# Revit family: Faucet-Handle-KOHLER-COMPONENTS-K-77981T
name_source: partatom
category: Plumbing Fixtures
revit_build: Autodesk Revit 2017 (Build: 20160225_1515(x64)
units: mm (PartAtom-declared; Revit-internal decimal feet)

## family parameters
Cut with Voids When Loaded = No
Host = Face
OmniClass Number = 23.31.11.00
OmniClass Title = Faucets
Part Type = Normal
Room Calculation Point = No
Round Connector Dimension = Use Diameter
Shared = No

## types (21) — shared parameters
ADA Compliant = No
Assembly Code = D2010
CW Connection = Yes
Cold Water Inlet = Cold Water Inlet
Date Modified = 09/08/2020
Default Elevation = 36"
Drain Included = No
Flow Rate = 0 GPM
HW Connection = Yes
Hot Water Inlet = Hot Water Inlet
Manufacturer = KOHLER Co.
Master Format 2014 = 22.41.39
Master Format 2014 Name = Residential Faucets, Supplies, and Trim
Material = Premium Metal Construction
Pressure = 0.00 psi
Product Documentation Link = https://files.kohler.com.cn
Product Name = COMPONENTS
Product Page URL = https://www.kohler.com.cn
URL = http://www.kohler.com.cn
Vent Connection = No
Waste Connection = No
Waste Water Outlet = Waste Water Outlet
WaterSense Certified = No

## per-type parameters (varying)
| type | Description | Dist | Dist_1 | Finish | Handle Clearance | Height | Ind Handle | Length | Lever Handle | Model | Oyl Handle | Type |
| Lever Handle, CP-Polished Chrome | Double-handle wall outlet basin faucet handle lever type | 0" | 2 3/8" | Kohler-Metal-CP-Polished_Chrome | 2 5/16" | 2 3/8" | No | 1 9/16" | Yes | K-77981T-4-CP | No | 1 |
| Lever Handle, BN-Roman Silver | Double-handle wall outlet basin faucet handle lever type | 0" | 2 3/8" | Kohler-Metal-BN-Roman_Silver | 2 5/16" | 2 3/8" | No | 1 9/16" | Yes | K-77981T-4-BN | No | 3 |
| Lever Handle, 2BL-Original Black | Double-handle wall outlet basin faucet handle lever type | 0" | 2 3/8" | Kohler-Metal-2BL-Original_Black | 2 5/16" | 2 3/8" | No | 1 9/16" | Yes | K-77981T-4-2BL | No | 5 |
| Oyl Handle, CP-Polished Chrome | Double-handle wall outlet basin faucet handle post type | 1 3/16" | 0" | Kohler-Metal-CP-Polished_Chrome | 2 3/8" | 2 3/8" | No | 1 1/2" | No | K-77981T-8-CP | Yes | 8 |
| Oyl Handle, BN-Roman Silver | Double-handle wall outlet basin faucet handle post type | 1 3/16" | 0" | Kohler-Metal-BN-Roman_Silver | 2 3/8" | 2 3/8" | No | 1 1/2" | No | K-77981T-8-BN | Yes | 10 |
| Oyl Handle, 2BL-Original_Black | Double-handle wall outlet basin faucet handle post type | 1 3/16" | 0" | Kohler-Metal-2BL-Original_Black | 2 3/8" | 2 3/8" | No | 1 1/2" | No | K-77981T-8-2BL | Yes | 12 |
| Industrial Handle, CP-Polished Chrome | Double Handle Wall Outlet Basin Faucet Handle-Wheel Type | 1 3/8" | 2 3/8" | Kohler-Metal-CP-Polished_Chrome | 2 3/4" | 2 3/4" | Yes | 1 3/4" | No | K-77981T-9-CP | No | 15 |
| Industrial Handle, BN-Roman Silver | Double Handle Wall Outlet Basin Faucet Handle-Wheel Type | 1 3/8" | 2 3/8" | Kohler-Metal-BN-Roman_Silver | 2 3/4" | 2 3/4" | Yes | 1 3/4" | No | K-77981T-9-BN | No | 17 |
| Industrial Handle,2MB-Vibrant Brushed Moderne Brass | Double Handle Wall Outlet Basin Faucet Handle-Wheel Type | 1 3/8" | 2 3/8" | Kohler-Metal-2MB-Vibrant_Brushed_Moderne_Brass | 2 3/4" | 2 3/4" | Yes | 1 3/4" | No | K-77981T-9-2MB | No | 21 |
| Lever Handle, AF-Flange Gold | Double-handle wall outlet basin faucet handle lever type | 0" | 2 3/8" | Kohler-Metal-AF-Flange_Gold | 2 5/16" | 2 3/8" | No | 1 9/16" | Yes | K-77981T-4-AF | No | 2 |
| Lever Handle, RGD-Rose Gold | Double-handle wall outlet basin faucet handle lever type | 0" | 2 3/8" | Kohler-Metal-RGD-Rose_Gold | 2 5/16" | 2 3/8" | No | 1 9/16" | Yes | K-77981T-4-RGD | No | 4 |
| Lever Handle, TT-Titanium Silver | Double-handle wall outlet basin faucet handle lever type | 0" | 2 3/8" | Kohler-Metal-TT-Titanium_Silver | 2 5/16" | 2 3/8" | No | 1 9/16" | Yes | K-77981T-4-TT | No | 6 |
| Oyl Handle, AF-Flange Gold | Double-handle wall outlet basin faucet handle post type | 1 3/16" | 0" | Kohler-Metal-AF-Flange_Gold | 2 3/8" | 2 3/8" | No | 1 1/2" | No | K-77981T-8-AF | Yes | 9 |
| Oyl Handle, RGD-Rose Gold | Double-handle wall outlet basin faucet handle post type | 1 3/16" | 0" | Kohler-Metal-RGD-Rose_Gold | 2 3/8" | 2 3/8" | No | 1 1/2" | No | K-77981T-8-RGD | Yes | 11 |
| Oyl Handle, TT-Titanium Silver | Double-handle wall outlet basin faucet handle post type | 1 3/16" | 0" | Kohler-Metal-TT-Titanium_Silver | 2 3/8" | 2 3/8" | No | 1 1/2" | No | K-77981T-8-TT | Yes | 13 |
| Industrial Handle, AF-Flange Gold | Double Handle Wall Outlet Basin Faucet Handle-Wheel Type | 1 3/8" | 2 3/8" | Kohler-Metal-AF-Flange_Gold | 2 3/4" | 2 3/4" | Yes | 1 3/4" | No | K-77981T-9-AF | No | 16 |
| Industrial Handle, RGD-Rose Gold | Double Handle Wall Outlet Basin Faucet Handle-Wheel Type | 1 3/8" | 2 3/8" | Kohler-Metal-RGD-Rose_Gold | 2 3/4" | 2 3/4" | Yes | 1 3/4" | No | K-77981T-9-RGD | No | 18 |
| Industrial Handle, 2BL-Original Black | Double Handle Wall Outlet Basin Faucet Handle-Wheel Type | 1 3/8" | 2 3/8" | Kohler-Metal-2BL-Original_Black | 2 3/4" | 2 3/4" | Yes | 1 3/4" | No | K-77981T-9-2BL | No | 19 |
| Industrial Handle, TT-Titanium Silver | Double Handle Wall Outlet Basin Faucet Handle-Wheel Type | 1 3/8" | 2 3/8" | Kohler-Metal-TT-Titanium_Silver | 2 3/4" | 2 3/4" | Yes | 1 3/4" | No | K-77981T-9-TT | No | 20 |
| Lever Handle,2MB-Vibrant Brushed Moderne Brass | Double-handle wall outlet basin faucet handle lever type | 0" | 2 3/8" | Kohler-Metal-2MB-Vibrant_Brushed_Moderne_Brass | 2 5/16" | 2 3/8" | No | 1 9/16" | Yes | K-77981T-4-2MB | No | 7 |
| Oyl Handle,2MB-Vibrant Brushed Moderne Brass | Double-handle wall outlet basin faucet handle post type | 1 3/16" | 0" | Kohler-Metal-2MB-Vibrant_Brushed_Moderne_Brass | 2 3/8" | 2 3/8" | No | 1 1/2" | No | K-77981T-8-2MB | Yes | 14 |

## geometry (parser evidence)
native form markers: Sweep x5
no freeform markers — native parametric forms only
